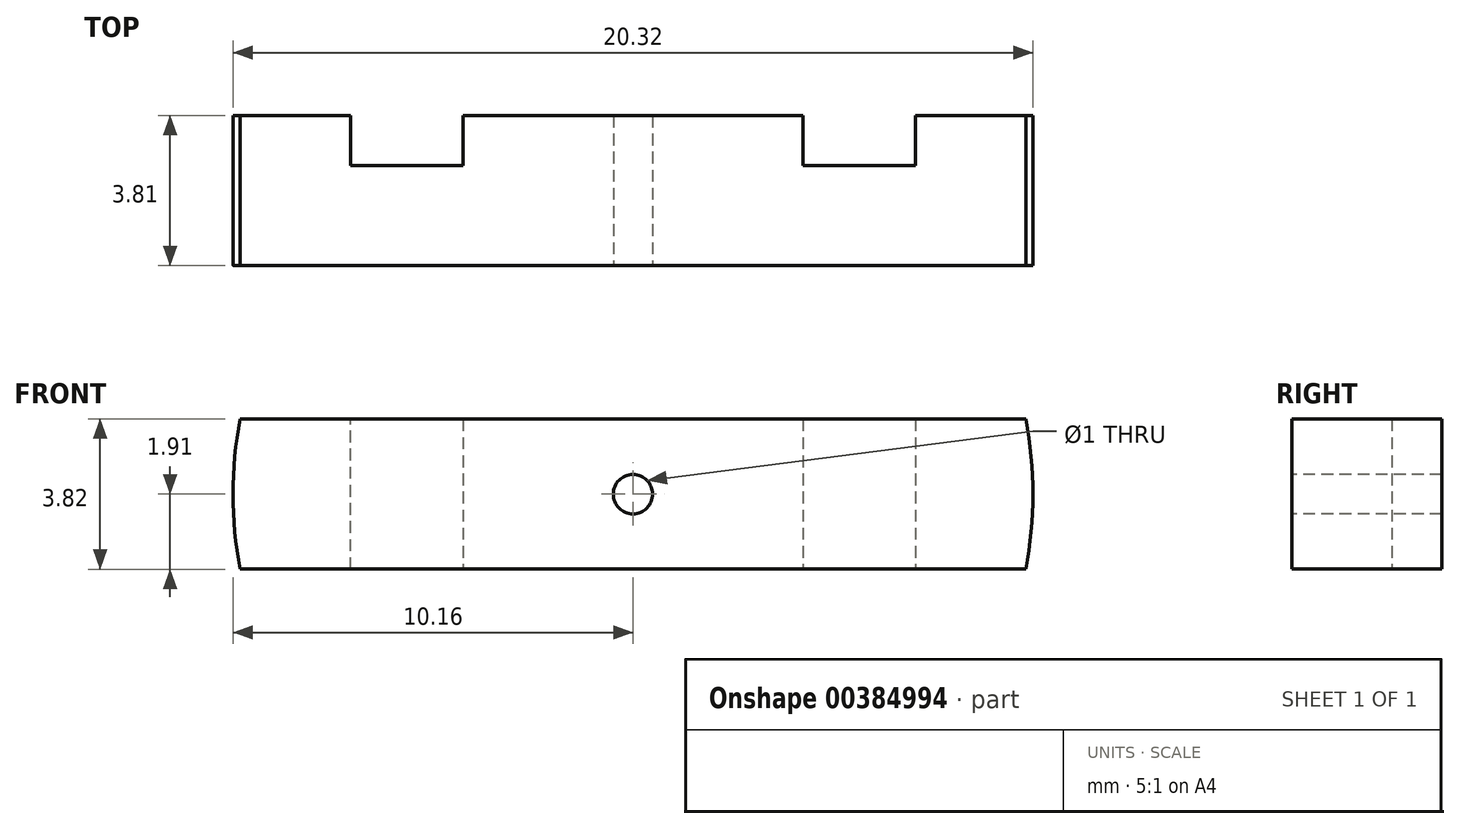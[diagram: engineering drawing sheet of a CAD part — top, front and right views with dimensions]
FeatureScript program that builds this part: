
annotation { "Feature Type Name" : "Feature", "Feature Type Description" : "" }
export const myFeature = defineFeature(function(context is Context, id is Id, definition is map)
    precondition{}
    {
        {
            var Q0;
            Q0=qCreatedBy(makeId("Front.planeOp"),FACE);
            var sketch = newSketch(context, id + "F0", { "sketchPlane" : qUnion([Q0])});
            skLineSegment(sketch, "E0", {"start": v(-9.98, 1.9) * mm, "end": v(9.98, 1.9) * mm});
            skLineSegment(sketch, "E1", {"start": v(-9.98, -1.9) * mm, "end": v(9.98, -1.9) * mm});
            skArc(sketch, "E2", {"start": v(-9.98, 1.9) * mm, "mid": v(-10.16, 0) * mm, "end": v(-9.98, -1.9) * mm});
            skArc(sketch, "E3", {"start": v(9.98, -1.9) * mm, "mid": v(10.16, 0) * mm, "end": v(9.98, 1.9) * mm});
            skCircle(sketch, "E4", {"center": v(0, 0) * mm, "radius": 10.8 * mm});
            skSolve(sketch);
        }
        {
            var Q0;
            Q0=makeQuery(id+"F0.imprint","IMPRINT",FACE,{"disambiguationData":[TD([[makeQuery(id+"F0.imprint","IMPRINT",EDGE,{"derivedFrom":sQuery(id+"F0.wireOp",EDGE,"E0")}),-1.0]])]});
            extrude(context, id + "F1", {"entities" : qUnion([Q0]), "depth" : 3.8 * mm, "offsetDistance" : 25.4 * mm});
        }
        {
            var Q0;
            Q0=makeQuery(id+"F1.opExtrude","CAP_FACE",FACE,{"disambiguationData":[OSD([sQuery(id+"F0.wireOp",EDGE,"E0"),sQuery(id+"F0.wireOp",EDGE,"E1"),sQuery(id+"F0.wireOp",EDGE,"E2"),sQuery(id+"F0.wireOp",EDGE,"E3")])],"isStart":false});
            var sketch = newSketch(context, id + "F2", { "sketchPlane" : qUnion([Q0])});
            skCircle(sketch, "E5", {"center": v(0, 0) * mm, "radius": 0.5 * mm});
            skSolve(sketch);
        }
        {
            var Q0;
            Q0=makeQuery(id+"F2.imprint","IMPRINT",FACE,{"disambiguationData":[TD([[makeQuery(id+"F2.imprint","IMPRINT",EDGE,{"derivedFrom":sQuery(id+"F2.wireOp",EDGE,"E5")}),1.0]])]});
            extrude(context, id + "F3", {"entities" : qUnion([Q0]), "operationType" : NewBodyOperationType.REMOVE, "oppositeDirection" : true, "depth" : 25.4 * mm, "offsetDistance" : 25.4 * mm});
        }
        {
            var Q0;
            Q0=makeQuery(id+"F0.imprint","IMPRINT",FACE,{"disambiguationData":[TD([[makeQuery(id+"F0.imprint","IMPRINT",EDGE,{"derivedFrom":sQuery(id+"F0.wireOp",EDGE,"E0")}),-1.0]])]});
            var sketch = newSketch(context, id + "F4", { "sketchPlane" : qUnion([Q0])});
            skLineSegment(sketch, "E6", {"start": v(4.32, 9.8) * mm, "end": v(4.32, -9.9) * mm});
            skLineSegment(sketch, "E7", {"start": v(7.18, 9.8) * mm, "end": v(7.18, -9.9) * mm});
            skLineSegment(sketch, "E8", {"start": v(4.32, 9.8) * mm, "end": v(7.18, 9.8) * mm});
            skLineSegment(sketch, "E9", {"start": v(7.18, -9.9) * mm, "end": v(4.32, -9.9) * mm});
            skLineSegment(sketch, "E10", {"start": v(-4.32, 9.9) * mm, "end": v(-4.32, -9.8) * mm});
            skLineSegment(sketch, "E11", {"start": v(-4.32, -9.8) * mm, "end": v(-7.18, -9.8) * mm});
            skLineSegment(sketch, "E12", {"start": v(-7.18, -9.8) * mm, "end": v(-7.18, 9.9) * mm});
            skLineSegment(sketch, "E13", {"start": v(-7.18, 9.9) * mm, "end": v(-4.32, 9.9) * mm});
            skLineSegment(sketch, "E14", {"start": v(0, 0) * mm, "end": v(4.32, -0.05) * mm});
            skLineSegment(sketch, "E15", {"start": v(0, 0) * mm, "end": v(-4.32, 0) * mm});
            skSolve(sketch);
        }
        {
            var Q0;
            {var subQ0=sQuery(id+"F4.wireOp",EDGE,"E6");var subQ1=makeQuery(id+"F0.imprint","IMPRINT",EDGE,{"derivedFrom":sQuery(id+"F0.wireOp",EDGE,"E0")});var subQ2=makeQuery(id+"F4.imprint","INTERSECT",VERTEX,{"derivedFrom":[subQ1,subQ0]});Q0=makeQuery(id+"F4.imprint","IMPRINT",FACE,{"disambiguationData":[TD([[makeQuery(id+"F4.imprint","IMPRINT",EDGE,{"disambiguationData":[TD([[subQ2,-1.0]])],"derivedFrom":subQ0}),1.0]])]});}
            var Q1;
            {var subQ0=sQuery(id+"F4.wireOp",EDGE,"E10");var subQ1=makeQuery(id+"F0.imprint","IMPRINT",EDGE,{"derivedFrom":sQuery(id+"F0.wireOp",EDGE,"E0")});var subQ2=makeQuery(id+"F4.imprint","INTERSECT",VERTEX,{"derivedFrom":[subQ1,subQ0]});Q1=makeQuery(id+"F4.imprint","IMPRINT",FACE,{"disambiguationData":[TD([[makeQuery(id+"F4.imprint","IMPRINT",EDGE,{"disambiguationData":[TD([[subQ2,-1.0]])],"derivedFrom":subQ0}),-1.0]])]});}
            extrude(context, id + "F5", {"entities" : qUnion([Q0, Q1]), "operationType" : NewBodyOperationType.REMOVE, "depth" : 1.27 * mm, "offsetDistance" : 25.4 * mm});
        }
    });
